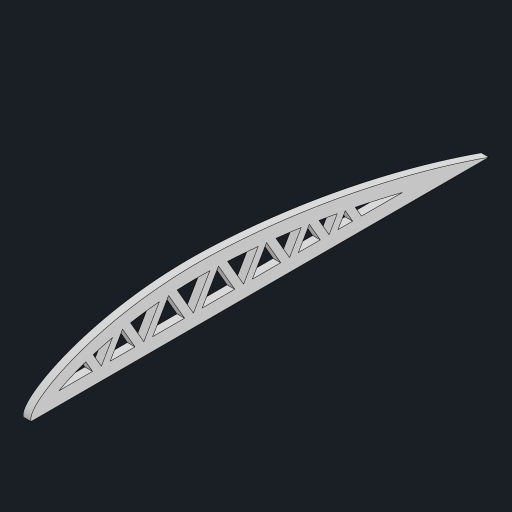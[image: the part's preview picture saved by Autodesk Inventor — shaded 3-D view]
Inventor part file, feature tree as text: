
AUTODESK INVENTOR PART (.ipt)
format: ipt  version: 2023 (Build 270158000, 158)  size: 201,728 bytes
history: native  units: mm
features: extrude x2, sketch x2, other x1
ambient origin geometry x8: Origin, YZ Plane, XZ Plane, XY Plane, X Axis, Y Axis, Z Axis, Center Point
bodies: Body1 (feature_tree)
feature tree (5):
  other  "ソリッド1"
  extrude  "押し出し1"  Depth=180.0mm
  extrude  "押し出し2"  Depth=3.0mm TaperAngle=0.0deg
  sketch  "スケッチ1"
  sketch  "スケッチ2"
